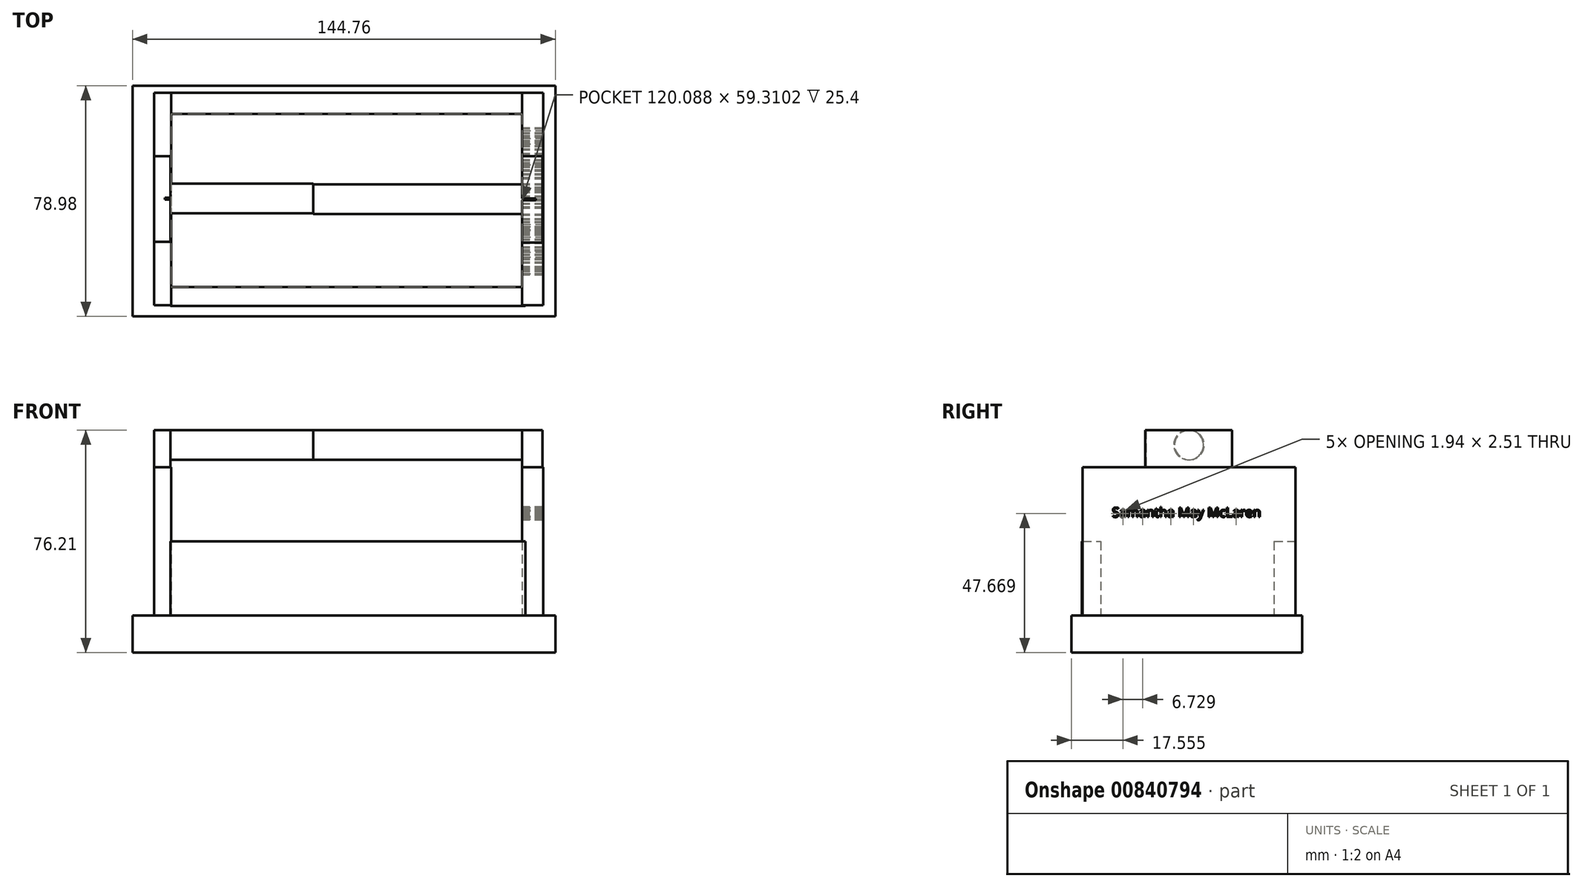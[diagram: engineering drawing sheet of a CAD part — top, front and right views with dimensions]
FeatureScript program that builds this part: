
annotation { "Feature Type Name" : "Feature", "Feature Type Description" : "" }
export const myFeature = defineFeature(function(context is Context, id is Id, definition is map)
    precondition{}
    {
        {
            var Q0;
            Q0=qCreatedBy(makeId("Top.planeOp"),FACE);
            var sketch = newSketch(context, id + "F0", { "sketchPlane" : qUnion([Q0])});
            skLineSegment(sketch, "E0.bottom", {"start": v(-61.8, 35.82) * mm, "end": v(82.95, 35.82) * mm});
            skLineSegment(sketch, "E0.top", {"start": v(-61.8, -43.16) * mm, "end": v(82.95, -43.16) * mm});
            skLineSegment(sketch, "E0.left", {"start": v(-61.8, 35.82) * mm, "end": v(-61.8, -43.16) * mm});
            skLineSegment(sketch, "E0.right", {"start": v(82.95, 35.82) * mm, "end": v(82.95, -43.16) * mm});
            skSolve(sketch);
        }
        {
            var Q0;
            Q0 = qSketchRegion(id + "F0", true);
            extrude(context, id + "F1", {"entities" : qUnion([Q0]), "oppositeDirection" : true, "depth" : 12.7 * mm, "offsetDistance" : 25.4 * mm});
        }
        {
            var Q0;
            Q0=qCreatedBy(makeId("Top.planeOp"),FACE);
            var sketch = newSketch(context, id + "F2", { "sketchPlane" : qUnion([Q0])});
            skLineSegment(sketch, "E1.bottom", {"start": v(-48.89, -33.18) * mm, "end": v(72.67, -33.18) * mm});
            skLineSegment(sketch, "E1.top", {"start": v(-48.89, -39.64) * mm, "end": v(72.67, -39.64) * mm});
            skLineSegment(sketch, "E1.left", {"start": v(-48.89, -33.18) * mm, "end": v(-48.89, -39.64) * mm});
            skLineSegment(sketch, "E1.right", {"start": v(72.67, -33.18) * mm, "end": v(72.67, -39.64) * mm});
            skLineSegment(sketch, "E2.bottom", {"start": v(-48.89, 26.13) * mm, "end": v(72.67, 26.13) * mm});
            skLineSegment(sketch, "E2.top", {"start": v(-48.89, 33.47) * mm, "end": v(72.67, 33.47) * mm});
            skLineSegment(sketch, "E2.left", {"start": v(-48.89, 26.13) * mm, "end": v(-48.89, 33.47) * mm});
            skLineSegment(sketch, "E2.right", {"start": v(72.67, 26.13) * mm, "end": v(72.67, 33.47) * mm});
            skSolve(sketch);
        }
        {
            var Q0;
            Q0 = qSketchRegion(id + "F2", true);
            extrude(context, id + "F3", {"entities" : qUnion([Q0]), "operationType" : NewBodyOperationType.ADD, "depth" : 25.4 * mm, "offsetDistance" : 25.4 * mm});
        }
        {
            var Q0;
            Q0=qCreatedBy(makeId("Top.planeOp"),FACE);
            var sketch = newSketch(context, id + "F4", { "sketchPlane" : qUnion([Q0])});
            skLineSegment(sketch, "E3.bottom", {"start": v(-48.6, 33.47) * mm, "end": v(-54.47, 33.47) * mm});
            skLineSegment(sketch, "E3.top", {"start": v(-48.6, -39.34) * mm, "end": v(-54.47, -39.34) * mm});
            skLineSegment(sketch, "E3.left", {"start": v(-48.6, 33.47) * mm, "end": v(-48.6, -39.34) * mm});
            skLineSegment(sketch, "E3.right", {"start": v(-54.47, 33.47) * mm, "end": v(-54.47, -39.34) * mm});
            skLineSegment(sketch, "E4.bottom", {"start": v(71.5, 33.47) * mm, "end": v(78.84, 33.47) * mm});
            skLineSegment(sketch, "E4.top", {"start": v(71.5, -39.34) * mm, "end": v(78.84, -39.34) * mm});
            skLineSegment(sketch, "E4.left", {"start": v(71.5, 33.47) * mm, "end": v(71.5, -39.34) * mm});
            skLineSegment(sketch, "E4.right", {"start": v(78.84, 33.47) * mm, "end": v(78.84, -39.34) * mm});
            skSolve(sketch);
        }
        {
            var Q0;
            Q0 = qSketchRegion(id + "F4", true);
            extrude(context, id + "F5", {"entities" : qUnion([Q0]), "operationType" : NewBodyOperationType.ADD, "depth" : 50.8 * mm, "offsetDistance" : 25.4 * mm});
        }
        {
            var Q0;
            Q0=qCreatedBy(makeId("Top.planeOp"),FACE);
            var sketch = newSketch(context, id + "F6", { "sketchPlane" : qUnion([Q0])});
            skLineSegment(sketch, "E5.bottom", {"start": v(-54.47, 11.74) * mm, "end": v(-48.89, 11.74) * mm});
            skLineSegment(sketch, "E5.top", {"start": v(-54.47, -17.62) * mm, "end": v(-48.89, -17.62) * mm});
            skLineSegment(sketch, "E5.left", {"start": v(-54.47, 11.74) * mm, "end": v(-54.47, -17.62) * mm});
            skLineSegment(sketch, "E5.right", {"start": v(-48.89, 11.74) * mm, "end": v(-48.89, -17.62) * mm});
            skLineSegment(sketch, "E6.bottom", {"start": v(71.5, 11.74) * mm, "end": v(78.54, 11.74) * mm});
            skLineSegment(sketch, "E6.top", {"start": v(71.5, -17.91) * mm, "end": v(78.54, -17.91) * mm});
            skLineSegment(sketch, "E6.left", {"start": v(71.5, 11.74) * mm, "end": v(71.5, -17.91) * mm});
            skLineSegment(sketch, "E6.right", {"start": v(78.54, 11.74) * mm, "end": v(78.54, -17.91) * mm});
            skSolve(sketch);
        }
        {
            var Q0;
            Q0 = qSketchRegion(id + "F6", true);
            extrude(context, id + "F7", {"entities" : qUnion([Q0]), "operationType" : NewBodyOperationType.ADD, "depth" : 63.5 * mm, "offsetDistance" : 25.4 * mm});
        }
        {
            var Q0;
            Q0=qCreatedBy(makeId("Right.planeOp"),FACE);
            var sketch = newSketch(context, id + "F8", { "sketchPlane" : qUnion([Q0])});
            skCircle(sketch, "E7", {"center": v(-3.08, 58.43) * mm, "radius": 5.08 * mm});
            skSolve(sketch);
        }
        {
            var Q0;
            Q0 = qSketchRegion(id + "F8", true);
            extrude(context, id + "F9", {"entities" : qUnion([Q0]), "operationType" : NewBodyOperationType.ADD, "depth" : 76.2 * mm, "offsetDistance" : 25.4 * mm});
        }
        {
            var Q0;
            Q0=qCreatedBy(makeId("Right.planeOp"),FACE);
            var sketch = newSketch(context, id + "F10", { "sketchPlane" : qUnion([Q0])});
            skCircle(sketch, "E8", {"center": v(-2.79, 58.43) * mm, "radius": 5.08 * mm});
            skSolve(sketch);
        }
        {
            var Q0;
            Q0 = qSketchRegion(id + "F10", true);
            extrude(context, id + "F11", {"entities" : qUnion([Q0]), "operationType" : NewBodyOperationType.ADD, "oppositeDirection" : true, "depth" : 50.8 * mm, "offsetDistance" : 25.4 * mm});
        }
        {
            var Q0;
            Q0=qCreatedBy(makeId("Right.planeOp"),FACE);
            var sketch = newSketch(context, id + "F12", { "sketchPlane" : qUnion([Q0])});
            skText(sketch, "E9", { "text": "Samantha May McLaren", "fontName": "OpenSans-Regular.ttf"});
            const initialGuessF12  = {"E9": [-0.02927, 0.03376, 1, 0, 0.00326]};
            skSetInitialGuess(sketch, initialGuessF12);
            skSolve(sketch);
        }
        {
            var Q0;
            Q0 = qSketchRegion(id + "F12", true);
            extrude(context, id + "F13", {"entities" : qUnion([Q0]), "operationType" : NewBodyOperationType.REMOVE, "depth" : 127 * mm, "offsetDistance" : 25.4 * mm});
        }
    });
